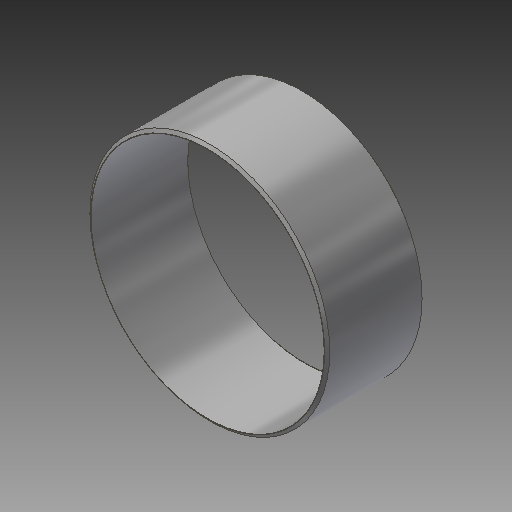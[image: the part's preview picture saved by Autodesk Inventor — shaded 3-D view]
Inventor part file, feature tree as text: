
AUTODESK INVENTOR PART (.ipt)
format: ipt  version: 2017.3 (Build 213257000, 257)  size: 120,320 bytes
history: native  units: in
note: dims shown in document units (in); Inventor stores cm internally (conversion verified against a paired STEP export)
features: chamfer x2, extrude x1, sketch x1
ambient origin geometry x8: Origin, YZ Plane, XZ Plane, XY Plane, X Axis, Y Axis, Z Axis, Center Point
bodies: Solid1 (feature_tree)
feature tree (4):
  extrude  "Extrusion1"  Depth=14.529in
  chamfer  "Chamfer1"  Distance=14.529in
  chamfer  "Chamfer2"  Distance=0.4375in
  sketch  "Sketch1"  dims[d0=36.0in d1=35.0in d2=14.529in d3=0.0in d4=0.4375in d5=0.125in d6=0.2577in d7=0.4375in d8=0.125in d9=0.2577in]
